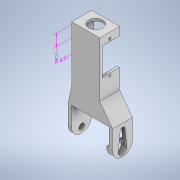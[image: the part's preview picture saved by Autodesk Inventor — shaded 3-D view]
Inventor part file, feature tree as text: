
AUTODESK INVENTOR PART (.ipt)
format: ipt  version: 2022.2 (Build 262287010, 287A)  size: 298,496 bytes
history: native  units: mm
features: extrude x15, sketch x15, other x3, fillet x1
ambient origin geometry x8: Origin, YZ Plane, XZ Plane, XY Plane, X Axis, Y Axis, Z Axis, Center Point
bodies: Solid1 (feature_tree)
feature tree (34):
  other  "Annotations"
  extrude  "Extrusion1"  Depth=60.0mm
  extrude  "Extrusion2"  Depth=2.0mm
  extrude  "Extrusion3"  Depth=15.0mm TaperAngle=0.0deg
  extrude  "Extrusion4"  Depth=2.0mm
  extrude  "Extrusion5"  Depth=8.5mm
  extrude  "Extrusion9"  Depth=3.0mm
  extrude  "Extrusion10"  Depth=15.0mm
  extrude  "Extrusion11"  Depth=2.0mm
  extrude  "Extrusion12"  Depth=15.0mm TaperAngle=0.0deg
  extrude  "Extrusion14"  Depth=5.0mm TaperAngle=0.0deg
  extrude  "Extrusion15"  TaperAngle=0.0deg  [1 undecoded]
  extrude  "Extrusion16"  Depth=3.0mm
  extrude  "Extrusion17"  TaperAngle=0.0deg  [1 undecoded]
  extrude  "Extrusion18"  Depth=5.0mm
  fillet  "Fillet2"  Radius=10.0mm
  extrude  "Extrusion19"  TaperAngle=90.0deg  [1 undecoded]
  sketch  "Sketch1"  dims[d0=24.0mm d1=60.0mm]
  sketch  "Sketch2"  dims[d2=2.0mm d3=0.0mm d4=2.0mm]
  sketch  "Sketch3"  dims[d5=2.0mm d6=15.0mm d7=0.0mm]
  sketch  "Sketch4"  dims[d8=2.0mm d9=2.0mm]
  sketch  "Sketch5"  dims[d10=8.5mm d11=8.5mm]
  sketch  "Sketch12"  dims[d12=27.5mm d13=3.0mm]
  sketch  "Sketch13"  dims[d14=12.0mm d15=0.0mm d23=15.0mm]
  sketch  "Sketch14"  dims[d24=23.5mm d25=2.0mm]
  sketch  "Sketch15"  dims[d26=2.0mm d27=15.0mm d28=0.0mm]
  sketch  "Sketch16"  dims[d29=5.0mm d30=5.0mm d31=0.0mm]
  sketch  "Sketch17"  dims[d32=8.6mm d33=0.0mm]
  sketch  "Sketch18"  dims[d51=38.0mm d52=3.0mm]
  sketch  "Sketch19"  dims[d53=25.0mm d54=0.0mm]
  sketch  "Sketch20"  dims[d55=3.0mm d56=5.0mm d57=10.0mm d58=0.0mm]
  sketch  "Sketch21"  dims[d59=15.0mm d60=90.0deg d61=10.0mm d62=0.0mm d63=15.0mm d64=90.0deg d65=5.0mm d66=8.5mm d67=20.0mm d68=20.0mm d69=0.0mm d70=2.0mm d71=10.0mm d72=0.0mm d75=10.0mm d76=0.0mm d77=2.0mm d78=0.0mm d79=2.0mm d80=0.0mm d81=12.0mm d82=12.0mm d83=8.5mm d84=2.0mm d85=0.0mm d86=7.5mm d87=10.0mm d88=0.0mm d89=8.5mm d90=4.0mm d91=15.0mm d92=0.0mm d93=3.0mm d94=0.0mm d95=2.0mm d96=15.0mm d36=6.779666mm d37=11.6mm d43=1.279577mm d44=8.5mm d97=0.5mm d98=0.872665mm]
  other  "Linear Dimension 1"
  other  "Linear Dimension 3"
note: 3 required parameter values undecoded (feature->parameter linkage not recoverable at this tier; creation-order binding heuristic only, values carry confidence <= 0.55)
